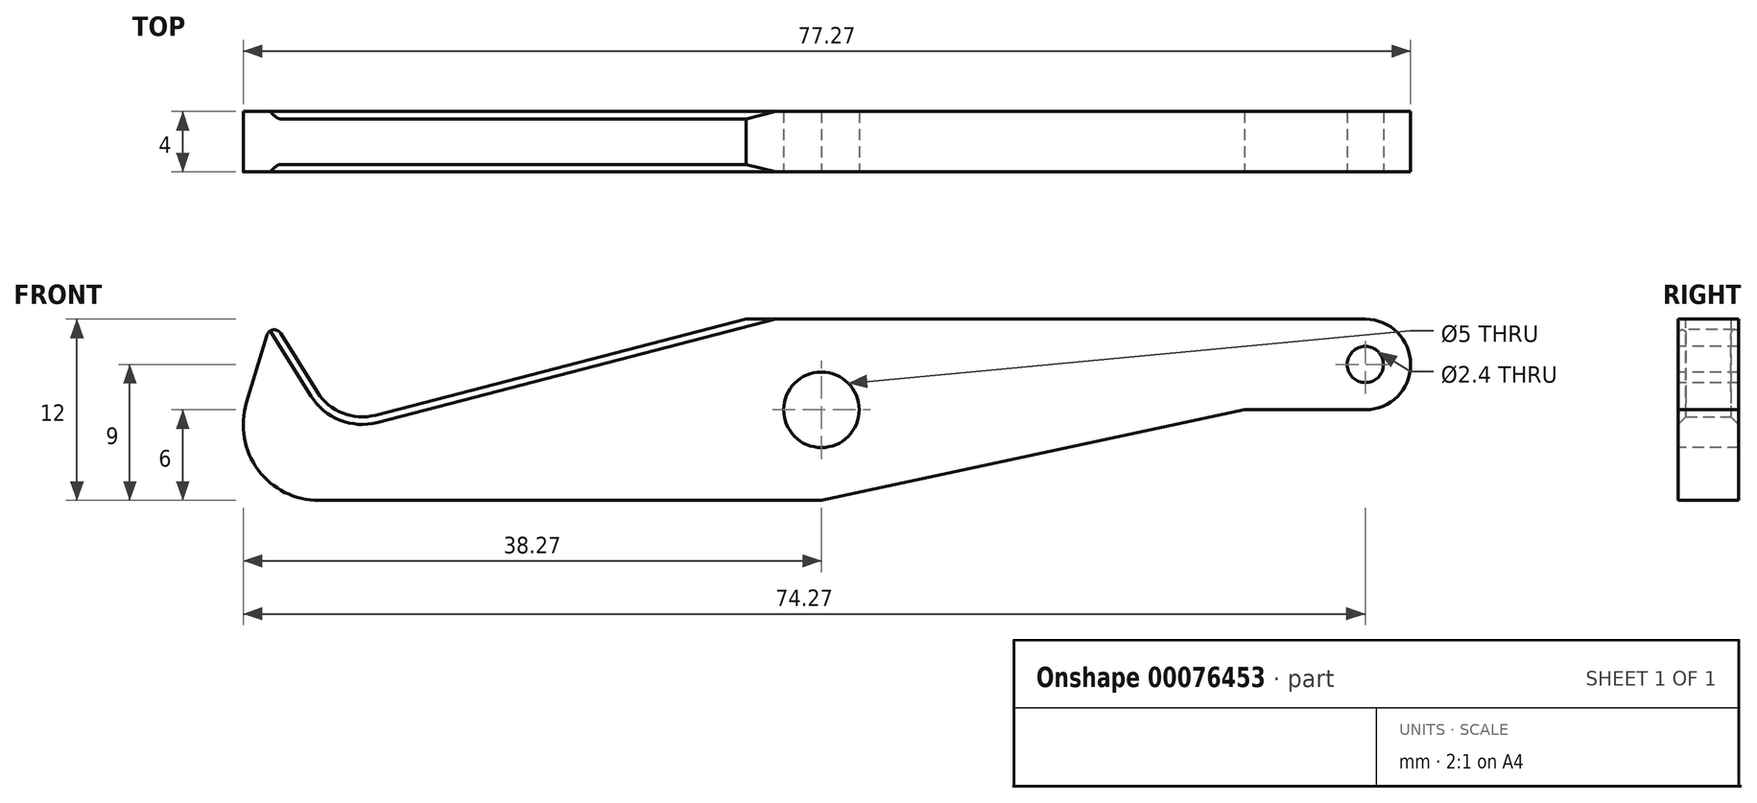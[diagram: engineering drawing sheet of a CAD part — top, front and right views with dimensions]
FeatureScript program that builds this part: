
annotation { "Feature Type Name" : "Feature", "Feature Type Description" : "" }
export const myFeature = defineFeature(function(context is Context, id is Id, definition is map)
    precondition{}
    {
        {
            var Q0;
            Q0=qCreatedBy(makeId("Front.planeOp"),FACE);
            var sketch = newSketch(context, id + "F0", { "sketchPlane" : qUnion([Q0])});
            skLineSegment(sketch, "E0", {"start": v(-28.14, 0) * mm, "end": v(40.5, 0) * mm, "construction": true});
            skLineSegment(sketch, "E1", {"start": v(0, 16.61) * mm, "end": v(0, -17.86) * mm, "construction": true});
            skLineSegment(sketch, "E2", {"start": v(-40, -6) * mm, "end": v(0, -6) * mm});
            skLineSegment(sketch, "E3", {"start": v(-5, 6) * mm, "end": v(-32, -1) * mm});
            skLineSegment(sketch, "E4", {"start": v(-32, -1) * mm, "end": v(-36.38, 6) * mm});
            skLineSegment(sketch, "E5.trimOffspring", {"start": v(-5, 6) * mm, "end": v(36, 6) * mm});
            skPoint(sketch, "E6", {"position": v(40.5, 0) * mm});
            skPoint(sketch, "E7", {"position": v(0, 0) * mm});
            skLineSegment(sketch, "E8", {"start": v(36, 0) * mm, "end": v(28, 0) * mm});
            skArc(sketch, "E9", {"start": v(36, 0) * mm, "mid": v(39, 3) * mm, "end": v(36, 6) * mm});
            skLineSegment(sketch, "E10", {"start": v(0, -6) * mm, "end": v(28, 0) * mm});
            skLineSegment(sketch, "E11", {"start": v(-36.38, 6) * mm, "end": v(-40, -6) * mm});
            skPoint(sketch, "E12.orphan", {"position": v(-32, -6) * mm});
            skSolve(sketch);
        }
        {
            var Q0;
            Q0=makeQuery(id+"F0.imprint","IMPRINT",FACE,{"disambiguationData":[TD([[makeQuery(id+"F0.imprint","IMPRINT",EDGE,{"derivedFrom":sQuery(id+"F0.wireOp",EDGE,"E2")}),1.0]])]});
            extrude(context, id + "F1", {"entities" : qUnion([Q0]), "oppositeDirection" : true, "depth" : 4 * mm});
        }
        {
            var Q0;
            Q0=sQuery(id+"F0.wireOp",VERTEX,"E7");
            var Q1;
            Q1=makeQuery(id+"F1.opExtrude","SWEPT_BODY",BODY,{"disambiguationData":[OSD([sQuery(id+"F0.wireOp",EDGE,"E2"),sQuery(id+"F0.wireOp",EDGE,"fPawsWhi-qPlZ-rODb-gOJh-qdvCDmw7WbbU"),sQuery(id+"F0.wireOp",EDGE,"E3"),sQuery(id+"F0.wireOp",EDGE,"E4"),sQuery(id+"F0.wireOp",EDGE,"965154d3-d1f7-4178-b76c-3ffb44e69379.trimOffspring"),sQuery(id+"F0.wireOp",EDGE,"E5.trimOffspring")])]});
            hole(context, id + "F2", {"style" : HoleStyle.SIMPLE, "endStyle" : HoleEndStyle.THROUGH, "standardTappedOrClearance" : lookupTablePath({ "standard" : "ISO", "size" : "5", "type" : "Drilled" }), "standardBlindInLast" : lookupTablePath({ "standard" : "ISO", "size" : "5", "type" : "Drilled" }), "holeDiameter" : 5 * mm, "locations" : qUnion([Q0]), "scope" : qUnion([Q1]), "isTappedThrough" : true});
        }
        {
            var Q0;
            Q0=makeQuery(id+"F1.opExtrude","SWEPT_EDGE",EDGE,{"disambiguationData":[OSD([sQuery(id+"F0.wireOp",EDGE,"E3"),sQuery(id+"F0.wireOp",EDGE,"E4")])]});
            fillet(context, id + "F3", {"entities" : qUnion([Q0]), "radius" : 3.5 * mm, "tangentPropagation" : true, "allowEdgeOverflow" : false});
        }
        {
            var Q0;
            Q0=sQuery(id+"F0.wireOp",VERTEX,"E9.center");
            var Q1;
            Q1=makeQuery(id+"F1.opExtrude","SWEPT_BODY",BODY,{"disambiguationData":[OSD([sQuery(id+"F0.wireOp",EDGE,"E2"),sQuery(id+"F0.wireOp",EDGE,"E3"),sQuery(id+"F0.wireOp",EDGE,"E4"),sQuery(id+"F0.wireOp",EDGE,"965154d3-d1f7-4178-b76c-3ffb44e69379.trimOffspring"),sQuery(id+"F0.wireOp",EDGE,"E5.trimOffspring"),sQuery(id+"F0.wireOp",EDGE,"E8"),sQuery(id+"F0.wireOp",EDGE,"E9"),sQuery(id+"F0.wireOp",EDGE,"E10")])]});
            hole(context, id + "F4", {"style" : HoleStyle.SIMPLE, "endStyle" : HoleEndStyle.THROUGH, "standardTappedOrClearance" : lookupTablePath({ "standard" : "ISO", "engagement" : "75%", "pitch" : "0.6 mm", "size" : "M3", "type" : "Tapped" }), "standardBlindInLast" : lookupTablePath({ "standard" : "ISO", "engagement" : "75%", "pitch" : "0.6 mm", "size" : "M3", "type" : "Tapped" }), "holeDiameter" : 2.4 * mm, "locations" : qUnion([Q0]), "scope" : qUnion([Q1]), "isTappedThrough" : true, "showTappedDepth" : true});
        }
        {
            var Q0;
            Q0=makeQuery(id+"F1.opExtrude","CAP_EDGE",EDGE,{"disambiguationData":[OSD([sQuery(id+"F0.wireOp",EDGE,"E4")])],"isStart":true});
            var Q1;
            Q1=makeQuery(id+"F1.opExtrude","CAP_EDGE",EDGE,{"disambiguationData":[OSD([sQuery(id+"F0.wireOp",EDGE,"E4")])],"isStart":false});
            chamfer(context, id + "F5", {"entities" : qUnion([Q0, Q1]), "width" : .5 * mm, "tangentPropagation" : true});
        }
        {
            var Q0;
            Q0=makeQuery(id+"F1.opExtrude","SWEPT_EDGE",EDGE,{"disambiguationData":[OSD([sQuery(id+"F0.wireOp",EDGE,"E2"),sQuery(id+"F0.wireOp",EDGE,"E11")])]});
            fillet(context, id + "F6", {"entities" : qUnion([Q0]), "radius" : 5 * mm, "tangentPropagation" : true, "allowEdgeOverflow" : false});
        }
        {
            var Q0;
            Q0=makeQuery(id+"F1.opExtrude","SWEPT_EDGE",EDGE,{"disambiguationData":[OSD([sQuery(id+"F0.wireOp",EDGE,"E4"),sQuery(id+"F0.wireOp",EDGE,"E11")])]});
            fillet(context, id + "F7", {"entities" : qUnion([Q0]), "radius" : .5 * mm, "tangentPropagation" : true, "allowEdgeOverflow" : false});
        }
    });
